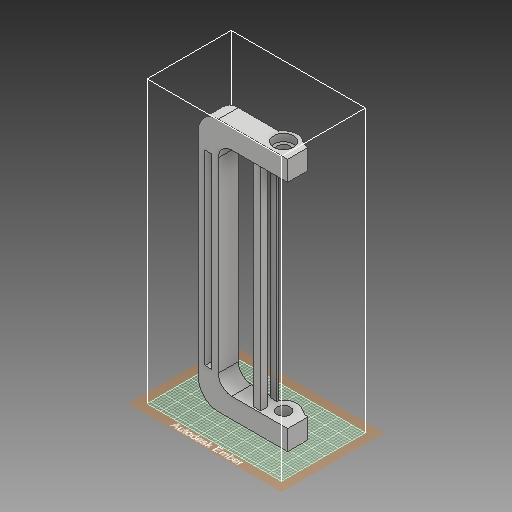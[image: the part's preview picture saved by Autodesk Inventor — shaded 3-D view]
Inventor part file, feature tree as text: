
AUTODESK INVENTOR PART (.ipt)
format: ipt  version: 2018 (Build 220112000, 112)  size: 475,136 bytes
history: native  units: in
note: dims shown in document units (in); Inventor stores cm internally (conversion verified against a paired STEP export)
features: sketch x27, extrude x17, fillet x7, hole x2, plane x1, mirror x1
ambient origin geometry x8: Origin, YZ Plane, XZ Plane, XY Plane, X Axis, Y Axis, Z Axis, Center Point
bodies: Solid1 (feature_tree)
feature tree (55):
  extrude  "Extrusion1"  Depth=0.375in
  sketch  "Sketch2"  dims[d3=0.375in d4=0.5in d5=0.375in d6=0.0in]
  extrude  "Extrusion2"  Depth=0.375in
  fillet  "Fillet1"  Radius=0.375in
  extrude  "Extrusion3"  Depth=0.375in
  extrude  "Extrusion4"  Depth=0.25in
  plane  "Work Plane1"
  mirror  "Mirror1"
  fillet  "Fillet2"  Radius=0.24in
  extrude  "Extrusion5"  Depth=0.375in
  sketch  "Sketch6"  dims[d17=1.0in d18=0.0in d19=0.24in d20=0.0in]
  extrude  "Extrusion6"  Depth=0.24in TaperAngle=0.0deg
  extrude  "Extrusion7"  Depth=0.375in
  fillet  "Fillet3"  Radius=0.25in
  fillet  "Fillet4"  Radius=0.375in
  fillet  "Fillet5"  Radius=0.25in
  fillet  "Fillet6"  Radius=0.125in
  sketch  "Sketch9"  dims[d30=0.125in d31=0.125in]
  extrude  "Extrusion8"  Depth=0.035in
  sketch  "Sketch11"  dims[d35=0.2in]
  sketch  "Sketch12"  dims[d36=0.2in d37=0.75in d38=0.375in d39=0.25in d40=0.5635in d41=0.35in d42=0.0in]
  hole  "Hole1"  [1 undecoded]
  hole  "Hole2"  [1 undecoded]
  sketch  "Sketch14"  dims[d51=3.5in d52=0.375in d53=0.0in]
  extrude  "Extrusion9"  Depth=0.125in
  sketch  "Sketch16"  dims[d58=0.4375in d59=0.0in d60=0.0625in d61=0.0in]
  extrude  "Extrusion10"  Depth=0.375in TaperAngle=0.0deg
  extrude  "Extrusion11"  Depth=0.25in
  extrude  "Extrusion12"  Depth=0.0625in TaperAngle=0.0deg
  sketch  "Sketch20"  dims[d72=0.375in d73=0.0in d74=0.4375in d75=0.0in]
  sketch  "Sketch21"  dims[d76=0.25in d77=0.4375in d78=0.0in]
  sketch  "Sketch22"
  extrude  "Extrusion13"  Depth=0.125in
  extrude  "Extrusion14"  Depth=0.25in TaperAngle=0.0deg
  fillet  "Fillet7"  Radius=0.25in
  extrude  "Extrusion15"  Depth=0.125in
  extrude  "Extrusion16"  Depth=0.4375in TaperAngle=0.0deg
  extrude  "Extrusion17"  Depth=0.4375in TaperAngle=0.0deg
  sketch  "Sketch1"  dims[d0=1.3in d1=0.375in]
  sketch  "Sketch3"  dims[d7=0.375in d8=0.0in d9=0.375in]
  sketch  "Sketch4"  dims[d10=0.24in d11=0.0in d12=0.25in d13=0.24in d14=0.0in]
  sketch  "Sketch5"  dims[d15=2.0in d16=0.375in]
  sketch  "Sketch7"  dims[d21=0.375in d22=0.0in d23=0.375in d24=0.25in d25=0.375in d26=0.25in d27=0.125in]
  sketch  "Sketch8"  dims[d28=0.035in d29=0.035in]
  sketch  "Sketch10"  dims[d32=4.375in d33=0.0in d34=0.2in]
  sketch  "Sketch13"  dims[d43=0.2in d44=0.75in d45=0.375in d46=0.25in d47=0.5635in d48=0.35in d49=0.0in d50=0.125in]
  sketch  "Sketch15"  dims[d56=0.25in d57=0.25in]
  sketch  "Sketch17"  dims[d62=0.04in d63=0.0in d64=0.125in]
  sketch  "Sketch18"  dims[d65=0.075in d66=4.04in d67=0.0in d68=0.25in]
  sketch  "Sketch19"  dims[d69=0.075in d70=0.0in d71=0.125in]
  sketch  "Sketch23"
  sketch  "Sketch24"
  sketch  "Sketch25"
  sketch  "Sketch26"
  sketch  "Sketch27"
note: 2 required parameter values undecoded (feature->parameter linkage not recoverable at this tier; creation-order binding heuristic only, values carry confidence <= 0.55)
